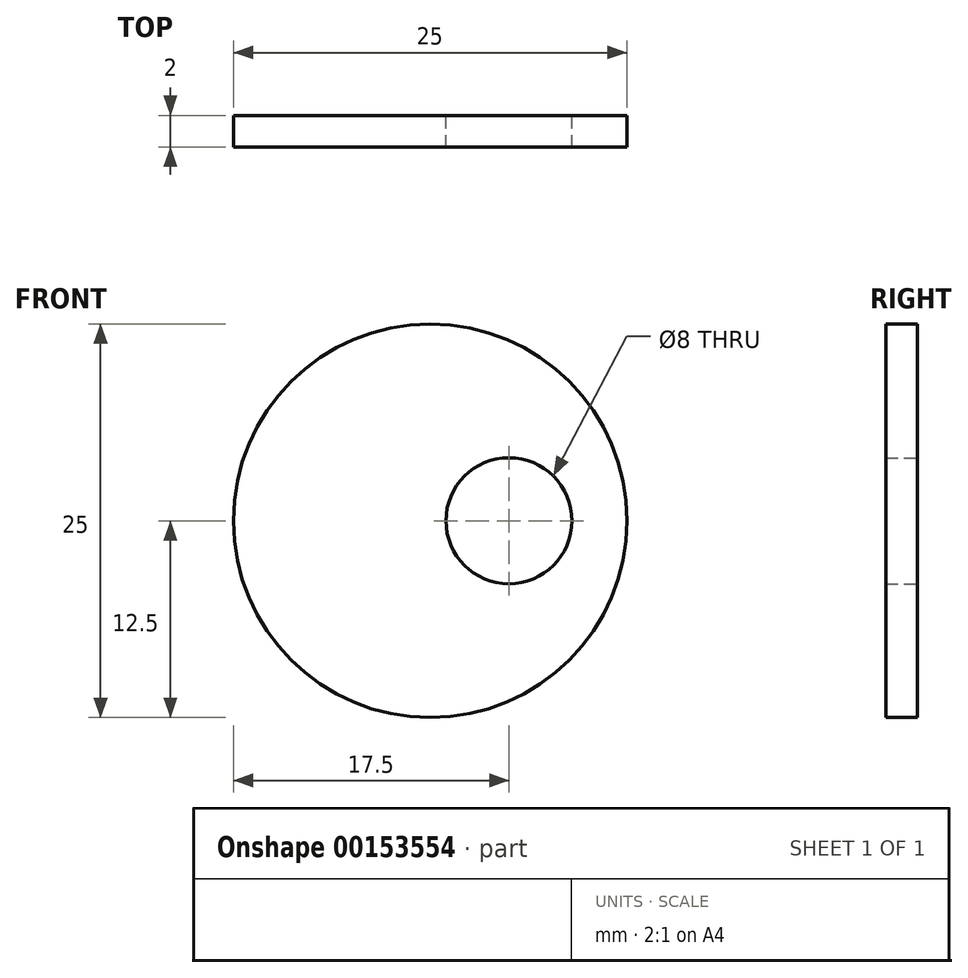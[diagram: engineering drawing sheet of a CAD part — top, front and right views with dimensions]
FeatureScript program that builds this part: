
annotation { "Feature Type Name" : "Feature", "Feature Type Description" : "" }
export const myFeature = defineFeature(function(context is Context, id is Id, definition is map)
    precondition{}
    {
        {
            var Q0;
            Q0=qCreatedBy(makeId("Front.planeOp"),FACE);
            var sketch = newSketch(context, id + "F0", { "sketchPlane" : qUnion([Q0])});
            skCircle(sketch, "E0", {"center": v(0, 0) * mm, "radius": 5 * mm, "construction": true});
            skCircle(sketch, "E1", {"center": v(0, 0) * mm, "radius": 12.5 * mm});
            skCircle(sketch, "E2", {"center": v(5, 0) * mm, "radius": 4 * mm});
            skLineSegment(sketch, "E3", {"start": v(0, 0) * mm, "end": v(5, 0) * mm, "construction": true});
            skSolve(sketch);
        }
        {
            var Q0;
            Q0 = qSketchRegion(id + "F0", true);
            extrude(context, id + "F1", {"entities" : qUnion([Q0]), "depth" : 2 * mm});
        }
    });
